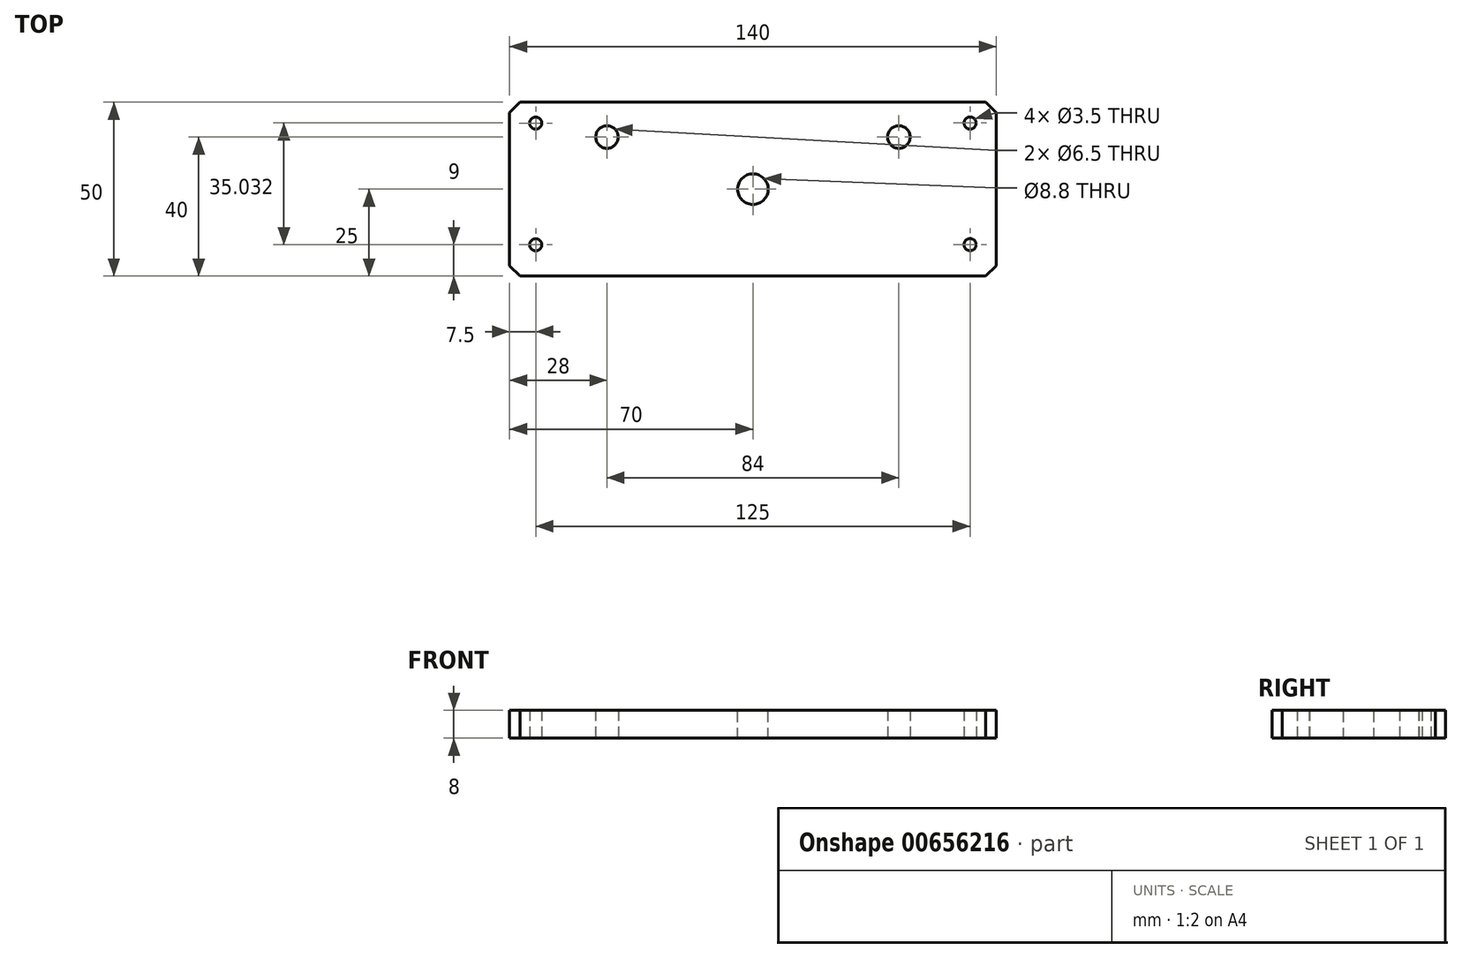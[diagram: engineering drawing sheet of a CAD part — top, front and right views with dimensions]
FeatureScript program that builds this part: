
annotation { "Feature Type Name" : "Feature", "Feature Type Description" : "" }
export const myFeature = defineFeature(function(context is Context, id is Id, definition is map)
    precondition{}
    {
        {
            var Q0;
            Q0=qCreatedBy(makeId("Top.planeOp"),FACE);
            var sketch = newSketch(context, id + "F0", { "sketchPlane" : qUnion([Q0])});
            skLineSegment(sketch, "E0.bottom", {"start": v(-70, 25) * mm, "end": v(70, 25) * mm});
            skLineSegment(sketch, "E0.top", {"start": v(-70, -25) * mm, "end": v(70, -25) * mm});
            skLineSegment(sketch, "E0.left", {"start": v(-70, 25) * mm, "end": v(-70, -25) * mm});
            skLineSegment(sketch, "E0.right", {"start": v(70, 25) * mm, "end": v(70, -25) * mm});
            skCircle(sketch, "E1", {"center": v(62.5, 19.03) * mm, "radius": 1.75 * mm});
            skLineSegment(sketch, "E2", {"start": v(62.5, 19.03) * mm, "end": v(-63.34, 19.03) * mm, "construction": true});
            skLineSegment(sketch, "E3", {"start": v(62.5, 19.03) * mm, "end": v(62.5, -20.81) * mm, "construction": true});
            skCircle(sketch, "E4.0.1.0", {"center": v(62.5, -15.97) * mm, "radius": 1.75 * mm});
            skCircle(sketch, "E4.1.0.0", {"center": v(-62.5, 19) * mm, "radius": 1.75 * mm});
            skCircle(sketch, "E4.1.1.0", {"center": v(-62.5, -16) * mm, "radius": 1.75 * mm});
            skLineSegment(sketch, "E4.direction1", {"start": v(62.5, 19.03) * mm, "end": v(-62.5, 19) * mm, "construction": true});
            skLineSegment(sketch, "E4.direction2", {"start": v(62.5, 19.03) * mm, "end": v(62.5, -15.97) * mm, "construction": true});
            skCircle(sketch, "E5", {"center": v(42, 15) * mm, "radius": 3.25 * mm});
            skCircle(sketch, "E6.MirrorC", {"center": v(-42, 15) * mm, "radius": 3.25 * mm});
            skCircle(sketch, "E7", {"center": v(0, 0) * mm, "radius": 2.5 * mm});
            skSolve(sketch);
        }
        {
            var Q0;
            Q0=qSketchRegion(id+"F0",true);
            extrude(context, id + "F1", {"entities" : qUnion([Q0]), "depth" : 8 * mm, "offsetDistance" : 25 * mm});
        }
        {
            var Q0;
            Q0=makeQuery(id+"F1.opExtrude","SWEPT_EDGE",EDGE,{"disambiguationData":[OSD([sQuery(id+"F0.wireOp",EDGE,"E0.top"),sQuery(id+"F0.wireOp",EDGE,"E0.left")])]});
            var Q1;
            Q1=makeQuery(id+"F1.opExtrude","SWEPT_EDGE",EDGE,{"disambiguationData":[OSD([sQuery(id+"F0.wireOp",EDGE,"E0.top"),sQuery(id+"F0.wireOp",EDGE,"E0.right")])]});
            var Q2;
            Q2=makeQuery(id+"F1.opExtrude","SWEPT_EDGE",EDGE,{"disambiguationData":[OSD([sQuery(id+"F0.wireOp",EDGE,"E0.bottom"),sQuery(id+"F0.wireOp",EDGE,"E0.right")])]});
            var Q3;
            Q3=makeQuery(id+"F1.opExtrude","SWEPT_EDGE",EDGE,{"disambiguationData":[OSD([sQuery(id+"F0.wireOp",EDGE,"E0.bottom"),sQuery(id+"F0.wireOp",EDGE,"E0.left")])]});
            chamfer(context, id + "F2", {"entities" : qUnion([Q0, Q1, Q2, Q3]), "width" : 3 * mm, "tangentPropagation" : true});
        }
        {
            var Q0;
            Q0=makeQuery(id+"F1.opExtrude","CAP_FACE",FACE,{"disambiguationData":[OSD([sQuery(id+"F0.wireOp",EDGE,"E0.bottom"),sQuery(id+"F0.wireOp",EDGE,"E0.top"),sQuery(id+"F0.wireOp",EDGE,"E0.left"),sQuery(id+"F0.wireOp",EDGE,"E0.right"),sQuery(id+"F0.wireOp",EDGE,"E1"),sQuery(id+"F0.wireOp",EDGE,"E4.0.1.0"),sQuery(id+"F0.wireOp",EDGE,"E4.1.0.0"),sQuery(id+"F0.wireOp",EDGE,"E4.1.1.0"),sQuery(id+"F0.wireOp",EDGE,"E5"),sQuery(id+"F0.wireOp",EDGE,"E6.MirrorC"),sQuery(id+"F0.wireOp",EDGE,"E7")])],"isStart":false});
            var sketch = newSketch(context, id + "F3", { "sketchPlane" : qUnion([Q0])});
            skCircle(sketch, "E8", {"center": v(0, 0) * mm, "radius": 5 * mm});
            skSolve(sketch);
        }
        {
            var Q0;
            Q0=sQuery(id+"F3.wireOp",VERTEX,"E8.center");
            var Q1;
            Q1=makeQuery(id+"F1.opExtrude","SWEPT_BODY",BODY,{"disambiguationData":[OSD([sQuery(id+"F0.wireOp",EDGE,"E0.bottom"),sQuery(id+"F0.wireOp",EDGE,"E0.top"),sQuery(id+"F0.wireOp",EDGE,"E0.left"),sQuery(id+"F0.wireOp",EDGE,"E0.right"),sQuery(id+"F0.wireOp",EDGE,"E1"),sQuery(id+"F0.wireOp",EDGE,"E4.0.1.0"),sQuery(id+"F0.wireOp",EDGE,"E4.1.0.0"),sQuery(id+"F0.wireOp",EDGE,"E4.1.1.0"),sQuery(id+"F0.wireOp",EDGE,"E5"),sQuery(id+"F0.wireOp",EDGE,"E6.MirrorC"),sQuery(id+"F0.wireOp",EDGE,"E7")])]});
            hole(context, id + "F4", {"style" : HoleStyle.SIMPLE, "endStyle" : HoleEndStyle.THROUGH, "standardTappedOrClearance" : lookupTablePath({ "standard" : "ISO", "engagement" : "75%", "pitch" : "1.25 mm", "size" : "M10", "type" : "Tapped" }), "standardBlindInLast" : lookupTablePath({ "standard" : "ISO", "engagement" : "75%", "pitch" : "1.25 mm", "size" : "M10", "type" : "Tapped" }), "holeDiameter" : 8.8 * mm, "majorDiameter" : 10 * mm, "showTappedDepth" : true, "isTappedThrough" : true, "tappedDepth" : 12 * mm, "tapClearance" : 3, "locations" : qUnion([Q0]), "scope" : qUnion([Q1])});
        }
    });
